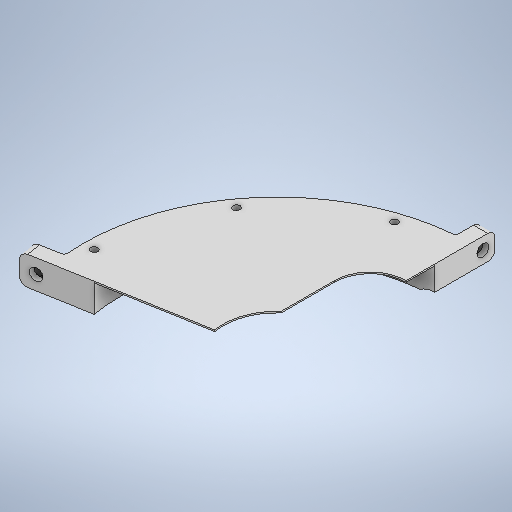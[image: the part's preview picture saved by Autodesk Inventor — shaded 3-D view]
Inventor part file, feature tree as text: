
AUTODESK INVENTOR PART (.ipt)
format: ipt  version: 2025 (Build 290162000, 162)  size: 411,136 bytes
history: native  units: in
note: dims shown in document units (in); Inventor stores cm internally (conversion verified against a paired STEP export)
features: sketch x15, extrude x11, hole x3, fillet x1
ambient origin geometry x8: Origin, YZ Plane, XZ Plane, XY Plane, X Axis, Y Axis, Z Axis, Center Point
bodies: Solid1 (feature_tree)
feature tree (30):
  extrude  "Extrusion1"  Depth=8.6614in
  extrude  "Extrusion2"  Depth=1.4173in
  extrude  "Extrusion3"  TaperAngle=0.0deg  [1 undecoded]
  extrude  "Extrusion4"  Depth=2.7559in
  hole  "Hole1"  [1 undecoded]
  extrude  "Extrusion5"  Depth=10.0394in
  extrude  "Extrusion6"  Depth=3.937in TaperAngle=360.0deg
  extrude  "Extrusion7"  Depth=0.3937in TaperAngle=0.0deg
  extrude  "Extrusion8"  Depth=0.5512in TaperAngle=0.0deg
  extrude  "Extrusion9"  TaperAngle=0.0deg  [1 undecoded]
  hole  "Hole2"  [1 undecoded]
  extrude  "Extrusion10"  Depth=0.1969in
  extrude  "Extrusion11"  Depth=0.3937in
  hole  "Hole3"  [1 undecoded]
  fillet  "Fillet2"  Radius=0.7874in
  sketch  "Sketch1"  dims[d0=10.6299in d1=8.6614in]
  sketch  "Sketch2"  dims[d5=0.1969in d6=0.0in d7=0.0in]
  sketch  "Sketch3"  dims[d8=0.7874in d9=0.0in d10=2.7559in]
  sketch  "Sketch4"  dims[d11=0.7874in d12=7.874in]
  sketch  "Sketch5"  dims[d13=0.0in d14=0.0in d15=10.0394in]
  sketch  "Sketch Circular Pattern1"  dims[d2=2.1654in d3=0.0in d4=1.4173in]
  sketch  "Sketch6"  dims[d16=0.1575in d17=3.937in d19=360.0deg]
  sketch  "Sketch7"  dims[d21=0.1969in d22=0.3937in d23=0.4094in d24=0.0787in d25=90.0deg d26=0.315in d27=0.8108in d28=0.5906in d29=0.0in]
  sketch  "Sketch8"  dims[d30=2.9528in d33=0.0394in d34=0.0in d38=0.5512in d39=0.0in]
  sketch  "Sketch9"  dims[d40=0.5497in d41=0.0in d42=0.0in]
  sketch  "Sketch10"  dims[d43=0.7677in d44=0.6693in]
  sketch  "Sketch11"  dims[d45=0.6693in d46=0.1969in]
  sketch  "Sketch12"  dims[d47=0.3937in d48=0.0in d49=0.3346in]
  sketch  "Sketch13"  dims[d50=0.3346in]
  sketch  "Sketch14"  dims[d51=0.3228in d52=0.2362in d53=0.5197in d54=0.2362in d55=90.0deg d56=0.315in d57=0.8108in d59=0.8858in d60=0.7874in d61=0.7874in d62=0.1969in d63=0.3937in d64=0.0in d65=0.3937in d66=0.3937in d67=0.5197in d68=0.2362in d69=0.0in d70=0.3937in d71=0.3937in d72=0.3228in d73=0.2362in d74=0.5197in d75=0.2362in d76=90.0deg d77=0.315in d78=0.8108in d79=0.0984in]
note: 5 required parameter values undecoded (feature->parameter linkage not recoverable at this tier; creation-order binding heuristic only, values carry confidence <= 0.55)
